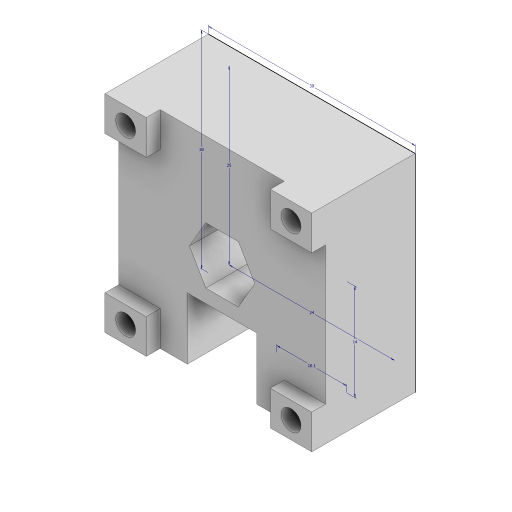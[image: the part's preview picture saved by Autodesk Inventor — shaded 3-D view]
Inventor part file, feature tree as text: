
AUTODESK INVENTOR PART (.ipt)
format: ipt  version: 2023 (Build 270158000, 158)  size: 181,248 bytes
history: native  units: mm
features: sketch x4, extrude x3, hole x2, projected_geometry x1
ambient origin geometry x8: Origin, YZ Plane, XZ Plane, XY Plane, X Axis, Y Axis, Z Axis, Center Point
bodies: Solid1 (feature_tree)
feature tree (10):
  sketch  "Sketch1"  dims[d0=30.0mm d1=30.0mm]
  extrude  "Extrusion1"  Depth=30.0mm
  hole  "Hole1"  [1 undecoded]
  hole  "Hole2"  [1 undecoded]
  extrude  "Extrusion2"  Depth=6.0mm
  extrude  "Extrusion3"  Depth=5.0mm
  sketch  "Sketch2"  dims[d2=20.0mm d4=24.0mm d5=20.0mm d7=25.0mm d10=10.1mm]
  sketch  "Sketch3"  dims[d11=14.0mm d12=15.0mm d13=0.0mm]
  projected_geometry  "Projected Loop1"
  sketch  "Sketch4"  dims[d14=2.9mm d15=6.0mm d16=12.6mm d17=2.0mm d18=90.0deg d19=8.0mm d20=20.594885mm d21=5.3mm d22=6.0mm d23=10.4mm d24=2.0mm d25=90.0deg d26=8.0mm d27=20.594885mm d28=6.0mm d29=5.0mm d30=6.0mm d31=5.0mm d32=6.0mm d33=5.0mm d34=2.0mm d35=0.0mm d36=8.2mm d37=10.0mm d38=0.0mm]
note: 2 required parameter values undecoded (feature->parameter linkage not recoverable at this tier; creation-order binding heuristic only, values carry confidence <= 0.55)
